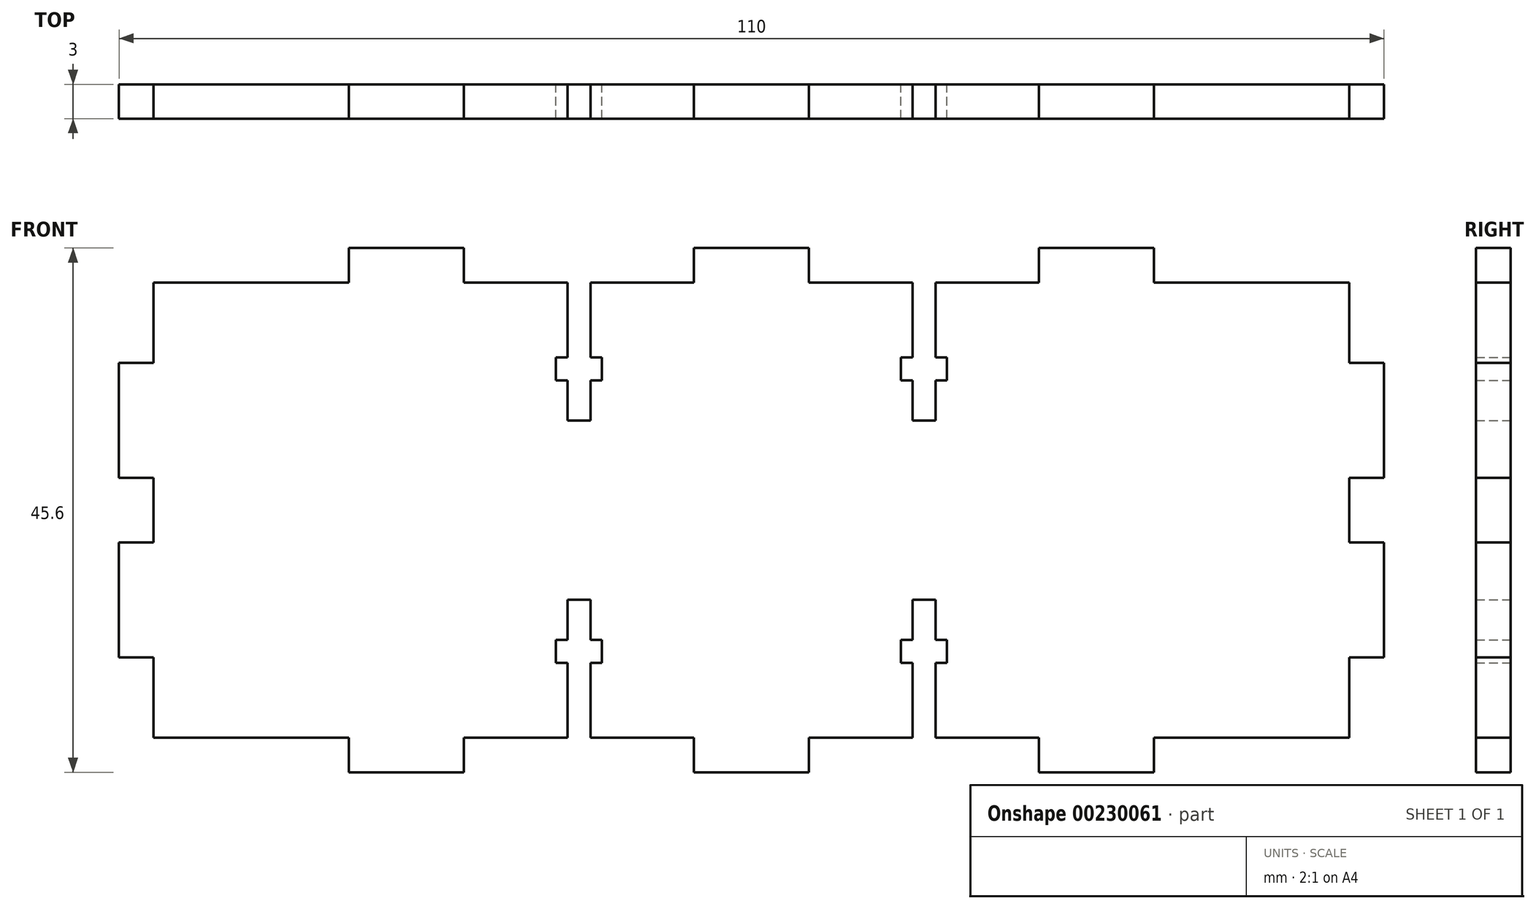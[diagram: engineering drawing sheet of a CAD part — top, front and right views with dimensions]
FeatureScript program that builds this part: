
annotation { "Feature Type Name" : "Feature", "Feature Type Description" : "" }
export const myFeature = defineFeature(function(context is Context, id is Id, definition is map)
    precondition{}
    {
        {
            var Q0;
            Q0=qCreatedBy(makeId("Front.planeOp"),FACE);
            var sketch = newSketch(context, id + "F0", { "sketchPlane" : qUnion([Q0])});
            skLineSegment(sketch, "E0", {"start": v(-52.31, 0) * mm, "end": v(-55.31, 0) * mm});
            skLineSegment(sketch, "E1", {"start": v(-52.31, 0) * mm, "end": v(-52.31, 2.8) * mm});
            skLineSegment(sketch, "E2", {"start": v(-52.31, 2.8) * mm, "end": v(-55.31, 2.8) * mm});
            skLineSegment(sketch, "E3", {"start": v(-55.31, 2.8) * mm, "end": v(-55.31, 12.8) * mm});
            skLineSegment(sketch, "E4", {"start": v(-55.31, 12.8) * mm, "end": v(-52.31, 12.8) * mm});
            skLineSegment(sketch, "E5", {"start": v(-52.31, 12.8) * mm, "end": v(-52.31, 19.8) * mm});
            skLineSegment(sketch, "E6", {"start": v(-52.31, 19.8) * mm, "end": v(-35.31, 19.8) * mm});
            skLineSegment(sketch, "E7", {"start": v(-35.31, 19.8) * mm, "end": v(-35.31, 22.8) * mm});
            skLineSegment(sketch, "E8", {"start": v(-35.31, 22.8) * mm, "end": v(-25.31, 22.8) * mm});
            skLineSegment(sketch, "E9", {"start": v(-25.31, 22.8) * mm, "end": v(-25.31, 19.8) * mm});
            skLineSegment(sketch, "E10", {"start": v(-25.31, 19.8) * mm, "end": v(-16.31, 19.8) * mm});
            skLineSegment(sketch, "E11", {"start": v(-5.31, 19.8) * mm, "end": v(-5.31, 22.8) * mm});
            skLineSegment(sketch, "E12", {"start": v(-5.31, 22.8) * mm, "end": v(-0.31, 22.8) * mm});
            skLineSegment(sketch, "E13", {"start": v(-15.31, 13.3) * mm, "end": v(-15.31, 0) * mm, "construction": true});
            skLineSegment(sketch, "E14.top", {"start": v(-16.31, 7.8) * mm, "end": v(-14.31, 7.8) * mm});
            skLineSegment(sketch, "E14.left", {"start": v(-16.31, 19.8) * mm, "end": v(-16.31, 13.3) * mm});
            skLineSegment(sketch, "E14.right", {"start": v(-14.31, 19.8) * mm, "end": v(-14.31, 13.3) * mm});
            skLineSegment(sketch, "E15.bottom", {"start": v(-17.31, 13.3) * mm, "end": v(-16.31, 13.3) * mm});
            skLineSegment(sketch, "E15.top", {"start": v(-17.31, 11.3) * mm, "end": v(-16.31, 11.3) * mm});
            skLineSegment(sketch, "E15.left", {"start": v(-17.31, 13.3) * mm, "end": v(-17.31, 11.3) * mm});
            skLineSegment(sketch, "E15.right", {"start": v(-13.31, 13.3) * mm, "end": v(-13.31, 11.3) * mm});
            skPoint(sketch, "E16.orphan", {"position": v(-15.31, 19.8) * mm});
            skLineSegment(sketch, "E17.trimOffspring", {"start": v(-14.31, 19.8) * mm, "end": v(-5.31, 19.8) * mm});
            skLineSegment(sketch, "E18.trimOffspring", {"start": v(-14.31, 13.3) * mm, "end": v(-13.31, 13.3) * mm});
            skLineSegment(sketch, "E19.trimOffspring", {"start": v(-14.31, 11.3) * mm, "end": v(-14.31, 7.8) * mm});
            skLineSegment(sketch, "E20.trimOffspring", {"start": v(-16.31, 11.3) * mm, "end": v(-16.31, 7.8) * mm});
            skLineSegment(sketch, "E21.trimOffspring", {"start": v(-14.31, 11.3) * mm, "end": v(-13.31, 11.3) * mm});
            skLineSegment(sketch, "E22", {"start": v(-0.31, 0) * mm, "end": v(-52.31, 0) * mm, "construction": true});
            skLineSegment(sketch, "E23.MirrorCS", {"start": v(-17.31, -11.3) * mm, "end": v(-16.31, -11.3) * mm});
            skLineSegment(sketch, "E24.MirrorCS", {"start": v(-14.31, -13.3) * mm, "end": v(-13.31, -13.3) * mm});
            skLineSegment(sketch, "E25.MirrorCS", {"start": v(-14.31, -11.3) * mm, "end": v(-13.31, -11.3) * mm});
            skLineSegment(sketch, "E26.MirrorCS", {"start": v(-17.31, -13.3) * mm, "end": v(-16.31, -13.3) * mm});
            skLineSegment(sketch, "E27.MirrorCS", {"start": v(-16.31, -7.8) * mm, "end": v(-14.31, -7.8) * mm});
            skLineSegment(sketch, "E28.MirrorCS", {"start": v(-52.31, 0) * mm, "end": v(-52.31, -2.8) * mm});
            skLineSegment(sketch, "E29.MirrorCS", {"start": v(-17.31, -13.3) * mm, "end": v(-17.31, -11.3) * mm});
            skLineSegment(sketch, "E30.MirrorCS", {"start": v(-14.31, -19.8) * mm, "end": v(-14.31, -13.3) * mm});
            skLineSegment(sketch, "E31.MirrorCS", {"start": v(-5.31, -19.8) * mm, "end": v(-5.31, -22.8) * mm});
            skLineSegment(sketch, "E32.MirrorCS", {"start": v(-5.31, -22.8) * mm, "end": v(-0.31, -22.8) * mm});
            skLineSegment(sketch, "E33.MirrorCS", {"start": v(-25.31, -19.8) * mm, "end": v(-16.31, -19.8) * mm});
            skLineSegment(sketch, "E34.MirrorCS", {"start": v(-13.31, -13.3) * mm, "end": v(-13.31, -11.3) * mm});
            skLineSegment(sketch, "E35.MirrorCS", {"start": v(-25.31, -22.8) * mm, "end": v(-25.31, -19.8) * mm});
            skLineSegment(sketch, "E36.MirrorCS", {"start": v(-35.31, -22.8) * mm, "end": v(-25.31, -22.8) * mm});
            skLineSegment(sketch, "E37.MirrorCS", {"start": v(-35.31, -19.8) * mm, "end": v(-35.31, -22.8) * mm});
            skLineSegment(sketch, "E38.MirrorCS", {"start": v(-52.31, -2.8) * mm, "end": v(-55.31, -2.8) * mm});
            skLineSegment(sketch, "E39.MirrorCS", {"start": v(-55.31, -2.8) * mm, "end": v(-55.31, -12.8) * mm});
            skLineSegment(sketch, "E40.MirrorCS", {"start": v(-14.31, -19.8) * mm, "end": v(-5.31, -19.8) * mm});
            skLineSegment(sketch, "E41.MirrorCS", {"start": v(-52.31, -12.8) * mm, "end": v(-52.31, -19.8) * mm});
            skLineSegment(sketch, "E42.MirrorCS", {"start": v(-16.31, -11.3) * mm, "end": v(-16.31, -7.8) * mm});
            skLineSegment(sketch, "E43.MirrorCS", {"start": v(-55.31, -12.8) * mm, "end": v(-52.31, -12.8) * mm});
            skLineSegment(sketch, "E44.MirrorCS", {"start": v(-52.31, -19.8) * mm, "end": v(-35.31, -19.8) * mm});
            skLineSegment(sketch, "E45.MirrorCS", {"start": v(-14.31, -11.3) * mm, "end": v(-14.31, -7.8) * mm});
            skLineSegment(sketch, "E46.MirrorCS", {"start": v(-16.31, -19.8) * mm, "end": v(-16.31, -13.3) * mm});
            skLineSegment(sketch, "E47.MirrorCS", {"start": v(-15.31, -13.3) * mm, "end": v(-15.31, 0) * mm, "construction": true});
            skPoint(sketch, "E48.MirrorP", {"position": v(-15.31, -19.8) * mm});
            skLineSegment(sketch, "E49", {"start": v(-0.31, 22.8) * mm, "end": v(-0.31, -22.8) * mm, "construction": true});
            skLineSegment(sketch, "E50.MirrorCS", {"start": v(16.69, -13.3) * mm, "end": v(15.69, -13.3) * mm});
            skLineSegment(sketch, "E51.MirrorCS", {"start": v(16.69, 13.3) * mm, "end": v(15.69, 13.3) * mm});
            skLineSegment(sketch, "E52.MirrorCS", {"start": v(16.69, -13.3) * mm, "end": v(16.69, -11.3) * mm});
            skLineSegment(sketch, "E53.MirrorCS", {"start": v(15.69, 7.8) * mm, "end": v(13.69, 7.8) * mm});
            skLineSegment(sketch, "E54.MirrorCS", {"start": v(51.69, 0) * mm, "end": v(54.69, 0) * mm});
            skLineSegment(sketch, "E55.MirrorCS", {"start": v(16.69, -11.3) * mm, "end": v(15.69, -11.3) * mm});
            skLineSegment(sketch, "E56.MirrorCS", {"start": v(12.69, -13.3) * mm, "end": v(12.69, -11.3) * mm});
            skLineSegment(sketch, "E57.MirrorCS", {"start": v(13.69, -11.3) * mm, "end": v(12.69, -11.3) * mm});
            skLineSegment(sketch, "E58.MirrorCS", {"start": v(16.69, 11.3) * mm, "end": v(15.69, 11.3) * mm});
            skLineSegment(sketch, "E59.MirrorCS", {"start": v(15.69, -7.8) * mm, "end": v(13.69, -7.8) * mm});
            skLineSegment(sketch, "E60.MirrorCS", {"start": v(13.69, -13.3) * mm, "end": v(12.69, -13.3) * mm});
            skLineSegment(sketch, "E61.MirrorCS", {"start": v(13.69, 13.3) * mm, "end": v(12.69, 13.3) * mm});
            skLineSegment(sketch, "E62.MirrorCS", {"start": v(13.69, 11.3) * mm, "end": v(12.69, 11.3) * mm});
            skLineSegment(sketch, "E63.MirrorCS", {"start": v(16.69, 13.3) * mm, "end": v(16.69, 11.3) * mm});
            skLineSegment(sketch, "E64.MirrorCS", {"start": v(51.69, 0) * mm, "end": v(51.69, 2.8) * mm});
            skLineSegment(sketch, "E65.MirrorCS", {"start": v(34.69, -19.8) * mm, "end": v(34.69, -22.8) * mm});
            skLineSegment(sketch, "E66.MirrorCS", {"start": v(-0.31, 0) * mm, "end": v(51.69, 0) * mm, "construction": true});
            skLineSegment(sketch, "E67.MirrorCS", {"start": v(15.69, -19.8) * mm, "end": v(15.69, -13.3) * mm});
            skLineSegment(sketch, "E68.MirrorCS", {"start": v(13.69, -19.8) * mm, "end": v(13.69, -13.3) * mm});
            skLineSegment(sketch, "E69.MirrorCS", {"start": v(14.69, 13.3) * mm, "end": v(14.69, 0) * mm, "construction": true});
            skLineSegment(sketch, "E70.MirrorCS", {"start": v(15.69, 19.8) * mm, "end": v(15.69, 13.3) * mm});
            skLineSegment(sketch, "E71.MirrorCS", {"start": v(51.69, 2.8) * mm, "end": v(54.69, 2.8) * mm});
            skPoint(sketch, "E72.MirrorP", {"position": v(14.69, -19.8) * mm});
            skLineSegment(sketch, "E73.MirrorCS", {"start": v(54.69, 2.8) * mm, "end": v(54.69, 12.8) * mm});
            skLineSegment(sketch, "E74.MirrorCS", {"start": v(54.69, 12.8) * mm, "end": v(51.69, 12.8) * mm});
            skLineSegment(sketch, "E75.MirrorCS", {"start": v(51.69, 12.8) * mm, "end": v(51.69, 19.8) * mm});
            skLineSegment(sketch, "E76.MirrorCS", {"start": v(51.69, 19.8) * mm, "end": v(34.69, 19.8) * mm});
            skLineSegment(sketch, "E77.MirrorCS", {"start": v(34.69, 19.8) * mm, "end": v(34.69, 22.8) * mm});
            skLineSegment(sketch, "E78.MirrorCS", {"start": v(34.69, 22.8) * mm, "end": v(24.69, 22.8) * mm});
            skLineSegment(sketch, "E79.MirrorCS", {"start": v(24.69, 22.8) * mm, "end": v(24.69, 19.8) * mm});
            skLineSegment(sketch, "E80.MirrorCS", {"start": v(24.69, 19.8) * mm, "end": v(15.69, 19.8) * mm});
            skLineSegment(sketch, "E81.MirrorCS", {"start": v(4.69, 19.8) * mm, "end": v(4.69, 22.8) * mm});
            skLineSegment(sketch, "E82.MirrorCS", {"start": v(4.69, 22.8) * mm, "end": v(-0.31, 22.8) * mm});
            skLineSegment(sketch, "E83.MirrorCS", {"start": v(51.69, -2.8) * mm, "end": v(54.69, -2.8) * mm});
            skLineSegment(sketch, "E84.MirrorCS", {"start": v(13.69, -11.3) * mm, "end": v(13.69, -7.8) * mm});
            skLineSegment(sketch, "E85.MirrorCS", {"start": v(13.69, 11.3) * mm, "end": v(13.69, 7.8) * mm});
            skLineSegment(sketch, "E86.MirrorCS", {"start": v(12.69, 13.3) * mm, "end": v(12.69, 11.3) * mm});
            skLineSegment(sketch, "E87.MirrorCS", {"start": v(13.69, -19.8) * mm, "end": v(4.69, -19.8) * mm});
            skLineSegment(sketch, "E88.MirrorCS", {"start": v(14.69, -13.3) * mm, "end": v(14.69, 0) * mm, "construction": true});
            skLineSegment(sketch, "E89.MirrorCS", {"start": v(51.69, -19.8) * mm, "end": v(34.69, -19.8) * mm});
            skLineSegment(sketch, "E90.MirrorCS", {"start": v(13.69, 19.8) * mm, "end": v(13.69, 13.3) * mm});
            skLineSegment(sketch, "E91.MirrorCS", {"start": v(4.69, -19.8) * mm, "end": v(4.69, -22.8) * mm});
            skLineSegment(sketch, "E92.MirrorCS", {"start": v(51.69, -12.8) * mm, "end": v(51.69, -19.8) * mm});
            skLineSegment(sketch, "E93.MirrorCS", {"start": v(4.69, -22.8) * mm, "end": v(-0.31, -22.8) * mm});
            skPoint(sketch, "E94.MirrorP", {"position": v(14.69, 19.8) * mm});
            skLineSegment(sketch, "E95.MirrorCS", {"start": v(13.69, 19.8) * mm, "end": v(4.69, 19.8) * mm});
            skLineSegment(sketch, "E96.MirrorCS", {"start": v(24.69, -19.8) * mm, "end": v(15.69, -19.8) * mm});
            skLineSegment(sketch, "E97.MirrorCS", {"start": v(15.69, 11.3) * mm, "end": v(15.69, 7.8) * mm});
            skLineSegment(sketch, "E98.MirrorCS", {"start": v(24.69, -22.8) * mm, "end": v(24.69, -19.8) * mm});
            skLineSegment(sketch, "E99.MirrorCS", {"start": v(34.69, -22.8) * mm, "end": v(24.69, -22.8) * mm});
            skLineSegment(sketch, "E100.MirrorCS", {"start": v(54.69, -2.8) * mm, "end": v(54.69, -12.8) * mm});
            skLineSegment(sketch, "E101.MirrorCS", {"start": v(15.69, -11.3) * mm, "end": v(15.69, -7.8) * mm});
            skLineSegment(sketch, "E102.MirrorCS", {"start": v(54.69, -12.8) * mm, "end": v(51.69, -12.8) * mm});
            skLineSegment(sketch, "E103.MirrorCS", {"start": v(51.69, 0) * mm, "end": v(51.69, -2.8) * mm});
            skSolve(sketch);
        }
        {
            var Q0;
            Q0 = qSketchRegion(id + "F0", true);
            extrude(context, id + "F1", {"entities" : qUnion([Q0]), "depth" : 3 * mm});
        }
    });
